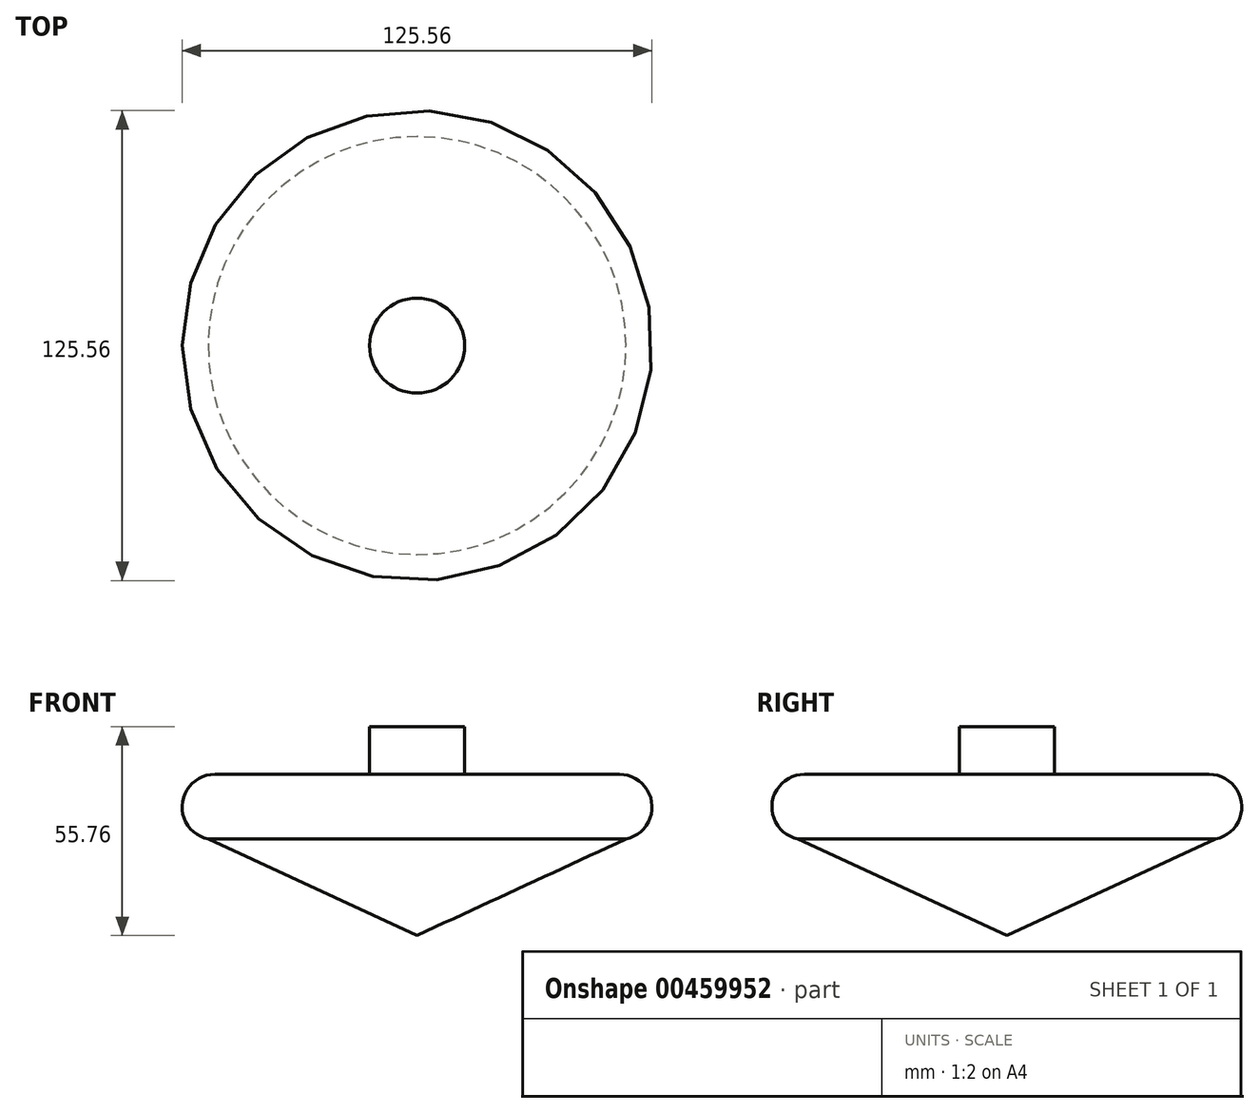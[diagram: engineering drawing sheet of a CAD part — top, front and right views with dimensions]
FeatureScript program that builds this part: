
annotation { "Feature Type Name" : "Feature", "Feature Type Description" : "" }
export const myFeature = defineFeature(function(context is Context, id is Id, definition is map)
    precondition{}
    {
        {
            var Q0;
            Q0=qCreatedBy(makeId("Front.planeOp"),FACE);
            var sketch = newSketch(context, id + "F0", { "sketchPlane" : qUnion([Q0])});
            skLineSegment(sketch, "E0", {"start": v(0, 0) * mm, "end": v(0, 55.73) * mm});
            skLineSegment(sketch, "E1", {"start": v(0, 43.01) * mm, "end": v(54.06, 43.01) * mm});
            skLineSegment(sketch, "E2", {"start": v(0, 25.57) * mm, "end": v(54.06, 25.57) * mm});
            skArc(sketch, "E3", {"start": v(54.06, 25.57) * mm, "mid": v(62.78, 34.3) * mm, "end": v(54.06, 43.01) * mm});
            skLineSegment(sketch, "E4", {"start": v(54.06, 25.57) * mm, "end": v(1.64, 0) * mm});
            skLineSegment(sketch, "E5", {"start": v(12.7, 43.01) * mm, "end": v(12.7, 55.76) * mm});
            skLineSegment(sketch, "E6", {"start": v(0, 55.73) * mm, "end": v(12.7, 55.76) * mm});
            skSolve(sketch);
        }
        {
            var Q0;
            {var subQ4=sQuery(id+"F0.wireOp",EDGE,"E5");Q0=makeQuery(id+"F0.imprint","IMPRINT",FACE,{"disambiguationData":[TD([[makeQuery(id+"F0.imprint","IMPRINT",EDGE,{"derivedFrom":subQ4}),1.0]])]});}
            var Q1;
            {var subQ0=sQuery(id+"F0.wireOp",EDGE,"E2");Q1=makeQuery(id+"F0.imprint","IMPRINT",FACE,{"disambiguationData":[TD([[makeQuery(id+"F0.imprint","IMPRINT",EDGE,{"derivedFrom":subQ0}),1.0]])]});}
            var Q2;
            Q2=sQuery(id+"F0.wireOp",EDGE,"E0");
            revolve(context, id + "F1", {"entities" : qUnion([Q0, Q1]), "axis" : qUnion([Q2]), "revolveType" : RevolveType.FULL});
        }
        {
            var Q0;
            Q0=qCreatedBy(makeId("Front.planeOp"),FACE);
            var sketch = newSketch(context, id + "F2", { "sketchPlane" : qUnion([Q0])});
            skLineSegment(sketch, "E7", {"start": v(0, 0) * mm, "end": v(57.04, 26.32) * mm});
            skLineSegment(sketch, "E8", {"start": v(0, 0) * mm, "end": v(0, 25.66) * mm});
            skLineSegment(sketch, "E9", {"start": v(0, 25.66) * mm, "end": v(57.04, 26.32) * mm});
            skSolve(sketch);
        }
        {
            var Q0;
            Q0=makeQuery(id+"F2.imprint","IMPRINT",FACE,{"disambiguationData":[TD([[makeQuery(id+"F2.imprint","IMPRINT",EDGE,{"derivedFrom":sQuery(id+"F2.wireOp",EDGE,"E7")}),1.0]])]});
            var Q1;
            Q1=sQuery(id+"F2.wireOp",EDGE,"E8");
            revolve(context, id + "F3", {"operationType" : NewBodyOperationType.ADD, "entities" : qUnion([Q0]), "axis" : qUnion([Q1]), "revolveType" : RevolveType.FULL});
        }
    });
